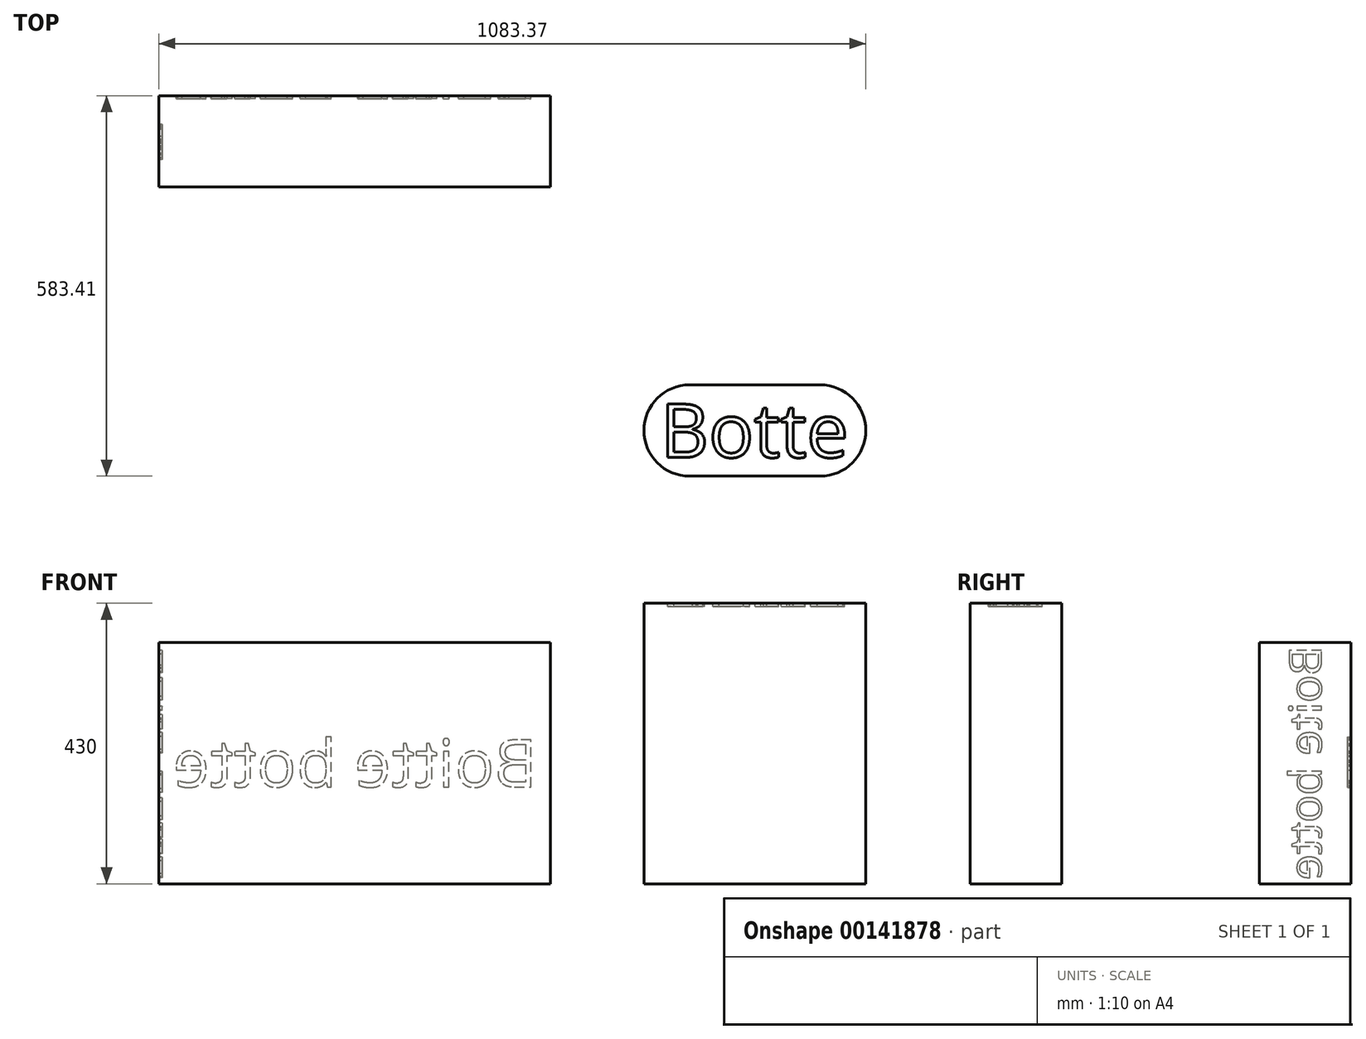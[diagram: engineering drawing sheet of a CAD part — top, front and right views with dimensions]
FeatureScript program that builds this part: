
annotation { "Feature Type Name" : "Feature", "Feature Type Description" : "" }
export const myFeature = defineFeature(function(context is Context, id is Id, definition is map)
    precondition{}
    {
        {
            var Q0;
            Q0=qCreatedBy(makeId("Top.planeOp"),FACE);
            var sketch = newSketch(context, id + "F0", { "sketchPlane" : qUnion([Q0])});
            skLineSegment(sketch, "E0.bottom", {"start": v(170, -70) * mm, "end": v(-170, -70) * mm});
            skLineSegment(sketch, "E0.top", {"start": v(170, 70) * mm, "end": v(-170, 70) * mm});
            skLineSegment(sketch, "E0.left", {"start": v(170, -70) * mm, "end": v(170, 70) * mm});
            skLineSegment(sketch, "E0.right", {"start": v(-170, -70) * mm, "end": v(-170, 70) * mm});
            skPoint(sketch, "E0.middle", {"position": v(0, 0) * mm});
            skSolve(sketch);
        }
        {
            var Q0;
            Q0=makeQuery(id+"F0.imprint","IMPRINT",FACE,{"disambiguationData":[TD([[makeQuery(id+"F0.imprint","IMPRINT",EDGE,{"derivedFrom":sQuery(id+"F0.wireOp",EDGE,"E0.bottom")}),-1.0]])]});
            extrude(context, id + "F1", {"entities" : qUnion([Q0]), "depth" : 430 * mm});
        }
        {
            var Q0;
            Q0=makeQuery(id+"F1.opExtrude","CAP_FACE",FACE,{"disambiguationData":[OSD([sQuery(id+"F0.wireOp",EDGE,"E0.bottom"),sQuery(id+"F0.wireOp",EDGE,"E0.top"),sQuery(id+"F0.wireOp",EDGE,"E0.left"),sQuery(id+"F0.wireOp",EDGE,"E0.right")])],"isStart":false});
            var sketch = newSketch(context, id + "F2", { "sketchPlane" : qUnion([Q0])});
            skText(sketch, "E1", { "text": "Botte", "fontName": "OpenSans-Regular.ttf"});
            skPoint(sketch, "E2", {"position": v(0, 0) * mm});
            const initialGuessF2  = {"E1": [-0.145, -0.04124, 1, 0, 0.08248]};
            skSetInitialGuess(sketch, initialGuessF2);
            skSolve(sketch);
        }
        {
            var Q0;
            Q0 = qSketchRegion(id + "F2", true);
            extrude(context, id + "F3", {"entities" : qUnion([Q0]), "operationType" : NewBodyOperationType.REMOVE, "oppositeDirection" : true, "depth" : 5 * mm});
        }
        {
            var Q0;
            Q0=makeQuery(id+"F1.opExtrude","SWEPT_EDGE",EDGE,{"disambiguationData":[OSD([sQuery(id+"F0.wireOp",EDGE,"E0.bottom"),sQuery(id+"F0.wireOp",EDGE,"E0.right")])]});
            var Q1;
            Q1=makeQuery(id+"F1.opExtrude","SWEPT_EDGE",EDGE,{"disambiguationData":[OSD([sQuery(id+"F0.wireOp",EDGE,"E0.top"),sQuery(id+"F0.wireOp",EDGE,"E0.right")])]});
            var Q2;
            Q2=makeQuery(id+"F1.opExtrude","SWEPT_EDGE",EDGE,{"disambiguationData":[OSD([sQuery(id+"F0.wireOp",EDGE,"E0.bottom"),sQuery(id+"F0.wireOp",EDGE,"E0.left")])]});
            var Q3;
            Q3=makeQuery(id+"F1.opExtrude","SWEPT_EDGE",EDGE,{"disambiguationData":[OSD([sQuery(id+"F0.wireOp",EDGE,"E0.top"),sQuery(id+"F0.wireOp",EDGE,"E0.left")])]});
            fillet(context, id + "F4", {"entities" : qUnion([Q0, Q1, Q2, Q3]), "radius" : 70 * mm, "tangentPropagation" : true, "allowEdgeOverflow" : false});
        }
        {
            var Q0;
            Q0=qCreatedBy(makeId("Top.planeOp"),FACE);
            var sketch = newSketch(context, id + "F5", { "sketchPlane" : qUnion([Q0])});
            skLineSegment(sketch, "E3.bottom", {"start": v(-313.37, 373.4) * mm, "end": v(-913.37, 373.4) * mm});
            skLineSegment(sketch, "E3.top", {"start": v(-313.37, 513.4) * mm, "end": v(-913.37, 513.4) * mm});
            skLineSegment(sketch, "E3.left", {"start": v(-313.37, 373.4) * mm, "end": v(-313.37, 513.4) * mm});
            skLineSegment(sketch, "E3.right", {"start": v(-913.37, 373.4) * mm, "end": v(-913.37, 513.4) * mm});
            skPoint(sketch, "E3.middle", {"position": v(-613.37, 443.4) * mm});
            skSolve(sketch);
        }
        {
            var Q0;
            Q0=makeQuery(id+"F5.imprint","IMPRINT",FACE,{"disambiguationData":[TD([[makeQuery(id+"F5.imprint","IMPRINT",EDGE,{"derivedFrom":sQuery(id+"F5.wireOp",EDGE,"E3.bottom")}),-1.0]])]});
            extrude(context, id + "F6", {"entities" : qUnion([Q0]), "depth" : 370 * mm});
        }
        {
            var Q0;
            Q0=makeQuery(id+"F6.opExtrude","SWEPT_FACE",FACE,{"disambiguationData":[OSD([sQuery(id+"F5.wireOp",EDGE,"E3.top")])]});
            var sketch = newSketch(context, id + "F7", { "sketchPlane" : qUnion([Q0])});
            skText(sketch, "E4", { "text": "Boitte botte", "fontName": "OpenSans-Regular.ttf"});
            skPoint(sketch, "E5", {"position": v(613.37, 185) * mm});
            skPoint(sketch, "E6", {"position": v(913.37, 185) * mm});
            const initialGuessF7  = {"E4": [0.33337, 0.14853, 1, 0, 0.07293]};
            skSetInitialGuess(sketch, initialGuessF7);
            skSolve(sketch);
        }
        {
            var Q0;
            Q0 = qSketchRegion(id + "F7", true);
            extrude(context, id + "F8", {"entities" : qUnion([Q0]), "operationType" : NewBodyOperationType.REMOVE, "oppositeDirection" : true, "depth" : 5 * mm});
        }
        {
            var Q0;
            Q0=makeQuery(id+"F6.opExtrude","SWEPT_FACE",FACE,{"disambiguationData":[OSD([sQuery(id+"F5.wireOp",EDGE,"E3.right")])]});
            var sketch = newSketch(context, id + "F9", { "sketchPlane" : qUnion([Q0])});
            skText(sketch, "E7", { "text": "Boite botte", "fontName": "OpenSans-Regular.ttf"});
            skPoint(sketch, "E8", {"position": v(-443.4, 185) * mm});
            skPoint(sketch, "E9", {"position": v(-443.4, 0) * mm});
            const initialGuessF9  = {"E7": [-0.46845, 0.365, 0, -1, 0.05008]};
            skSetInitialGuess(sketch, initialGuessF9);
            skSolve(sketch);
        }
        {
            var Q0;
            Q0 = qSketchRegion(id + "F9", true);
            extrude(context, id + "F10", {"entities" : qUnion([Q0]), "operationType" : NewBodyOperationType.REMOVE, "oppositeDirection" : true, "depth" : 5 * mm});
        }
    });
